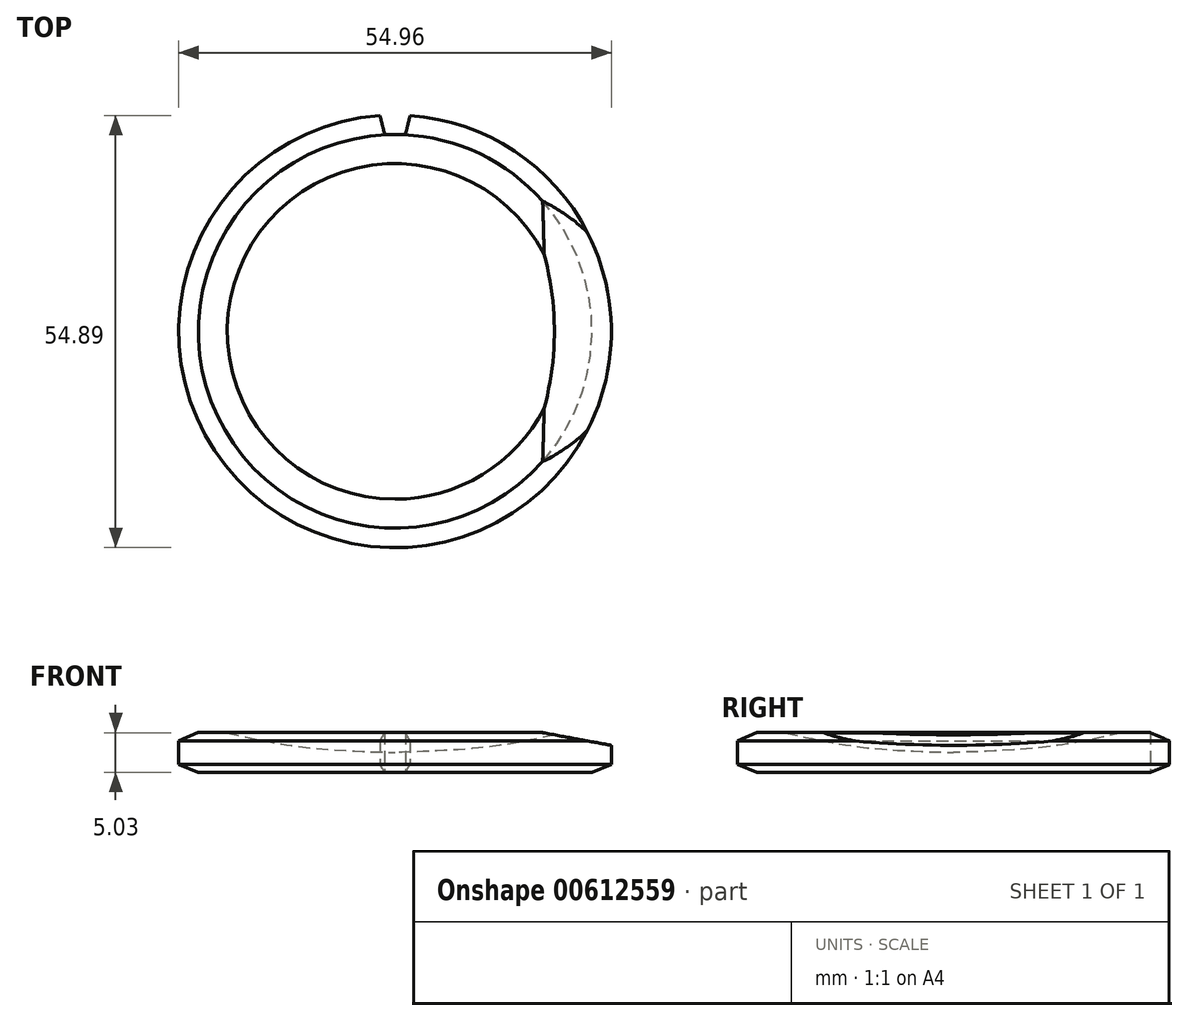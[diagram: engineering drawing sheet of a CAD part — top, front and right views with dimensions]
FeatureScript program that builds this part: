
annotation { "Feature Type Name" : "Feature", "Feature Type Description" : "" }
export const myFeature = defineFeature(function(context is Context, id is Id, definition is map)
    precondition{}
    {
        {
            var Q0;
            Q0=qCreatedBy(makeId("Right.planeOp"),FACE);
            var sketch = newSketch(context, id + "F0", { "sketchPlane" : qUnion([Q0])});
            skLineSegment(sketch, "E0.bottom", {"start": v(0, 0) * mm, "end": v(-25, 0) * mm});
            skLineSegment(sketch, "E0.left", {"start": v(0, 0) * mm, "end": v(0, 2.5) * mm});
            skLineSegment(sketch, "E0.right", {"start": v(-25, 0) * mm, "end": v(-25, 0) * mm});
            skPoint(sketch, "E1.third.point", {"position": v(-27.48, 2.52) * mm});
            skPoint(sketch, "E1.third.point.positionSnap0", {"position": v(-25, 2.52) * mm});
            skFitSpline(sketch, "E2", {"points": [v(-21.31, 5) * mm, v(-12.2, 3.27) * mm, v(0, 2.5) * mm], "startDerivative": vector(18.82, -4.26) * mm, "endDerivative": vector(23.69, -0.82) * mm});
            skLineSegment(sketch, "E3", {"start": v(-21.31, 5) * mm, "end": v(-25, 5.03) * mm});
            skLineSegment(sketch, "E4", {"start": v(-25, 5.03) * mm, "end": v(-25, 5.03) * mm});
            skLineSegment(sketch, "E5", {"start": v(-25, 0) * mm, "end": v(-27.48, 0.98) * mm});
            skLineSegment(sketch, "E6", {"start": v(-27.48, 0.98) * mm, "end": v(-27.48, 3.98) * mm});
            skLineSegment(sketch, "E7", {"start": v(-27.48, 3.98) * mm, "end": v(-25, 5.03) * mm});
            skSolve(sketch);
        }
        {
            var Q0;
            {var subQ1=sQuery(id+"F0.wireOp",EDGE,"E0.bottom");Q0=makeQuery(id+"F0.imprint","IMPRINT",FACE,{"disambiguationData":[TD([[makeQuery(id+"F0.imprint","IMPRINT",EDGE,{"derivedFrom":subQ1}),-1.0]])]});}
            var Q1;
            Q1=sQuery(id+"F0.wireOp",EDGE,"E0.left");
            revolve(context, id + "F1", {"entities" : qUnion([Q0]), "axis" : qUnion([Q1]), "revolveType" : RevolveType.FULL});
        }
        {
            var Q0;
            Q0=qCreatedBy(makeId("Top.planeOp"),FACE);
            var sketch = newSketch(context, id + "F2", { "sketchPlane" : qUnion([Q0])});
            skPoint(sketch, "E8.0.midPoint", {"position": v(0, 24.98) * mm});
            skLineSegment(sketch, "E9", {"start": v(1.31, 24.98) * mm, "end": v(2.46, 29.62) * mm});
            skLineSegment(sketch, "E10.MirrorCS", {"start": v(-1.31, 24.98) * mm, "end": v(-2.46, 29.62) * mm});
            skLineSegment(sketch, "E11", {"start": v(-2.46, 29.62) * mm, "end": v(2.46, 29.62) * mm});
            skLineSegment(sketch, "E12", {"start": v(1.31, 24.98) * mm, "end": v(-1.31, 24.98) * mm});
            skSolve(sketch);
        }
        {
            var Q0;
            Q0=makeQuery(id+"F2.imprint","IMPRINT",FACE,{"disambiguationData":[TD([[makeQuery(id+"F2.imprint","IMPRINT",EDGE,{"derivedFrom":sQuery(id+"F2.wireOp",EDGE,"E9")}),1.0]])]});
            var Q1;
            Q1=sQuery(id+"F2.wireOp",EDGE,"E8.4");
            var Q2;
            Q2=sQuery(id+"F2.wireOp",EDGE,"E8.0");
            var Q3;
            Q3=sQuery(id+"F2.wireOp",EDGE,"E8.1");
            extrude(context, id + "F3", {"entities" : qUnion([Q0]), "operationType" : NewBodyOperationType.REMOVE, "surfaceEntities" : qUnion([Q1, Q2, Q3]), "depth" : 6 * mm, "offsetDistance" : 25 * mm});
        }
        {
            var Q0;
            Q0=qCreatedBy(makeId("Front.planeOp"),FACE);
            var sketch = newSketch(context, id + "F4", { "sketchPlane" : qUnion([Q0])});
            skLineSegment(sketch, "E13", {"start": v(0, 8.5) * mm, "end": v(32.48, 2.5) * mm});
            skLineSegment(sketch, "E14", {"start": v(32.48, 2.5) * mm, "end": v(32.48, 7.9) * mm});
            skLineSegment(sketch, "E15", {"start": v(32.48, 7.9) * mm, "end": v(0, 13.5) * mm});
            skLineSegment(sketch, "E16", {"start": v(0, 13.5) * mm, "end": v(0, 8.5) * mm});
            skSolve(sketch);
        }
        {
            var Q0;
            Q0 = qSketchRegion(id + "F4", true);
            extrude(context, id + "F5", {"entities" : qUnion([Q0]), "operationType" : NewBodyOperationType.REMOVE, "oppositeDirection" : true, "depth" : 40 * mm, "offsetDistance" : 25 * mm, "hasSecondDirection" : true, "secondDirectionOppositeDirection" : false, "secondDirectionDepth" : 40 * mm});
        }
    });
